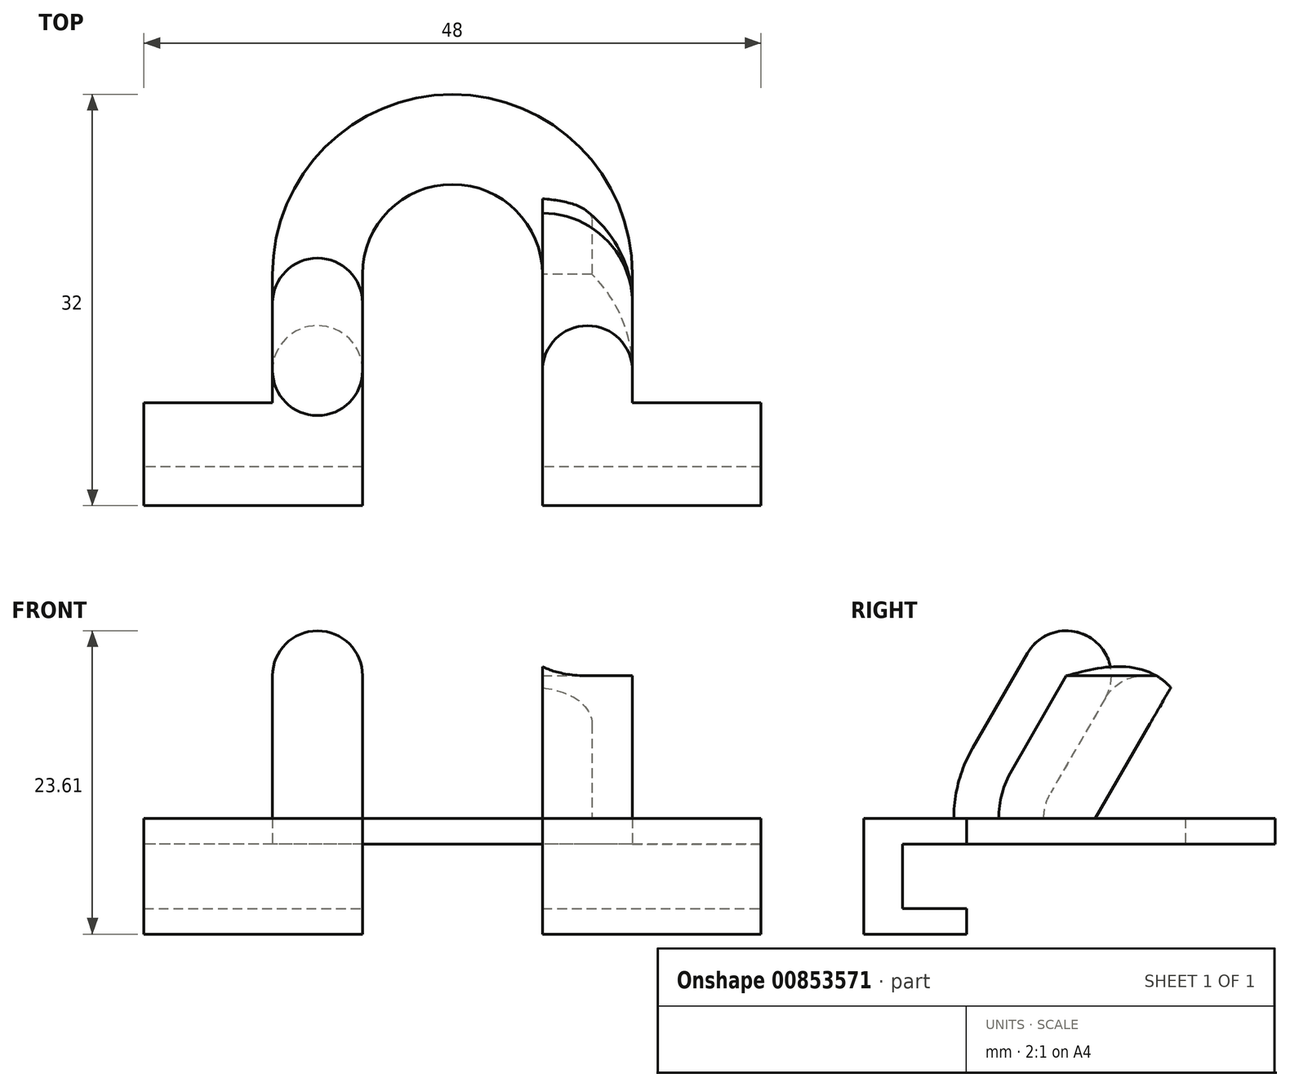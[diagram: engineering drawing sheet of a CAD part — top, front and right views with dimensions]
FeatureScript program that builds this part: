
annotation { "Feature Type Name" : "Feature", "Feature Type Description" : "" }
export const myFeature = defineFeature(function(context is Context, id is Id, definition is map)
    precondition{}
    {
        {
            var Q0;
            Q0=qCreatedBy(makeId("Top.planeOp"),FACE);
            var sketch = newSketch(context, id + "F0", { "sketchPlane" : qUnion([Q0])});
            skLineSegment(sketch, "E0.bottom", {"start": v(0, 0) * mm, "end": v(14, 0) * mm});
            skLineSegment(sketch, "E0.left", {"start": v(0, 0) * mm, "end": v(0, 15) * mm});
            skLineSegment(sketch, "E0.right", {"start": v(14, 0) * mm, "end": v(14, 15) * mm});
            skArc(sketch, "E1", {"start": v(14, 15) * mm, "mid": v(7, 22) * mm, "end": v(0, 15) * mm});
            skArc(sketch, "E2.0", {"start": v(21, 15) * mm, "mid": v(7, 29) * mm, "end": v(-7, 15) * mm});
            skLineSegment(sketch, "E3", {"start": v(0, 0) * mm, "end": v(-7, 0) * mm});
            skLineSegment(sketch, "E4", {"start": v(14, 0) * mm, "end": v(21, 0) * mm});
            skLineSegment(sketch, "E5", {"start": v(21, -3) * mm, "end": v(-7, -3) * mm});
            skLineSegment(sketch, "E6", {"start": v(0, 0) * mm, "end": v(0, -3) * mm});
            skLineSegment(sketch, "E7", {"start": v(14, 0) * mm, "end": v(14, -3) * mm});
            skLineSegment(sketch, "E8", {"start": v(0, 15) * mm, "end": v(-7, 15) * mm});
            skLineSegment(sketch, "E9", {"start": v(21, 15) * mm, "end": v(14, 15) * mm});
            skLineSegment(sketch, "E10", {"start": v(-17, 5) * mm, "end": v(-17, 0) * mm});
            skLineSegment(sketch, "E11", {"start": v(-17, 0) * mm, "end": v(-17, -3) * mm});
            skLineSegment(sketch, "E12", {"start": v(-17, -3) * mm, "end": v(-7, -3) * mm});
            skLineSegment(sketch, "E13", {"start": v(-7, 0) * mm, "end": v(-17, 0) * mm});
            skLineSegment(sketch, "E14", {"start": v(31, 5) * mm, "end": v(31, 0) * mm});
            skLineSegment(sketch, "E15", {"start": v(31, 0) * mm, "end": v(21, 0) * mm});
            skLineSegment(sketch, "E16", {"start": v(31, -3) * mm, "end": v(31, 0) * mm});
            skLineSegment(sketch, "E17", {"start": v(21, -3) * mm, "end": v(31, -3) * mm});
            skLineSegment(sketch, "E18", {"start": v(21, 15) * mm, "end": v(21, 5) * mm});
            skLineSegment(sketch, "E19", {"start": v(21, 5) * mm, "end": v(31, 5) * mm});
            skLineSegment(sketch, "E20", {"start": v(-7, 15) * mm, "end": v(-7, 5) * mm});
            skLineSegment(sketch, "E21", {"start": v(-7, 5) * mm, "end": v(-17, 5) * mm});
            skLineSegment(sketch, "E22", {"start": v(-7, 5) * mm, "end": v(0, 5) * mm});
            skLineSegment(sketch, "E23", {"start": v(21, 5) * mm, "end": v(14, 5) * mm});
            skSolve(sketch);
        }
        {
            var Q0;
            {var subQ0=sQuery(id+"F0.wireOp",EDGE,"E4");Q0=makeQuery(id+"F0.imprint","IMPRINT",FACE,{"disambiguationData":[TD([[makeQuery(id+"F0.imprint","IMPRINT",EDGE,{"derivedFrom":subQ0}),1.0]])]});}
            var Q1;
            {var subQ0=sQuery(id+"F0.wireOp",EDGE,"E3");Q1=makeQuery(id+"F0.imprint","IMPRINT",FACE,{"disambiguationData":[TD([[makeQuery(id+"F0.imprint","IMPRINT",EDGE,{"derivedFrom":subQ0}),-1.0]])]});}
            extrude(context, id + "F1", {"entities" : qUnion([Q0, Q1]), "depth" : 2 * mm, "offsetDistance" : 25 * mm});
        }
        {
            var Q0;
            Q0=makeQuery(id+"F0.imprint","IMPRINT",FACE,{"disambiguationData":[TD([[makeQuery(id+"F0.imprint","IMPRINT",EDGE,{"derivedFrom":sQuery(id+"F0.wireOp",EDGE,"E0.left")}),1.0]])]});
            var Q1;
            Q1=makeQuery(id+"F0.imprint","IMPRINT",FACE,{"disambiguationData":[TD([[makeQuery(id+"F0.imprint","IMPRINT",EDGE,{"derivedFrom":sQuery(id+"F0.wireOp",EDGE,"E1")}),-1.0]])]});
            var Q2;
            Q2=makeQuery(id+"F0.imprint","IMPRINT",FACE,{"disambiguationData":[TD([[makeQuery(id+"F0.imprint","IMPRINT",EDGE,{"derivedFrom":sQuery(id+"F0.wireOp",EDGE,"E0.right")}),-1.0]])]});
            var Q3;
            {var subQ0=sQuery(id+"F0.wireOp",EDGE,"E4");Q3=makeQuery(id+"F0.imprint","IMPRINT",FACE,{"disambiguationData":[TD([[makeQuery(id+"F0.imprint","IMPRINT",EDGE,{"derivedFrom":subQ0}),1.0]])]});}
            var Q4;
            {var subQ0=sQuery(id+"F0.wireOp",EDGE,"E3");Q4=makeQuery(id+"F0.imprint","IMPRINT",FACE,{"disambiguationData":[TD([[makeQuery(id+"F0.imprint","IMPRINT",EDGE,{"derivedFrom":subQ0}),-1.0]])]});}
            extrude(context, id + "F2", {"entities" : qUnion([Q0, Q1, Q2, Q3, Q4]), "depth" : 9 * mm, "offsetDistance" : 25 * mm, "hasSecondDirection" : true, "secondDirectionOppositeDirection" : false, "secondDirectionDepth" : 7 * mm});
        }
        {
            var Q0;
            {var subQ3=sQuery(id+"F0.wireOp",EDGE,"E3");Q0=makeQuery(id+"F0.imprint","IMPRINT",FACE,{"disambiguationData":[TD([[makeQuery(id+"F0.imprint","IMPRINT",EDGE,{"derivedFrom":subQ3}),1.0]])]});}
            var Q1;
            {var subQ3=sQuery(id+"F0.wireOp",EDGE,"E4");Q1=makeQuery(id+"F0.imprint","IMPRINT",FACE,{"disambiguationData":[TD([[makeQuery(id+"F0.imprint","IMPRINT",EDGE,{"derivedFrom":subQ3}),-1.0]])]});}
            extrude(context, id + "F3", {"entities" : qUnion([Q0, Q1]), "depth" : 9 * mm, "offsetDistance" : 25 * mm});
        }
        {
            var Q0;
            Q0=makeQuery(id+"F1.opExtrude","SWEPT_BODY",BODY,{"disambiguationData":[OSD([sQuery(id+"F0.wireOp",EDGE,"E0.left"),sQuery(id+"F0.wireOp",EDGE,"E0.right"),sQuery(id+"F0.wireOp",EDGE,"E1"),sQuery(id+"F0.wireOp",EDGE,"E2.0"),sQuery(id+"F0.wireOp",EDGE,"E2.1"),sQuery(id+"F0.wireOp",EDGE,"E2.3"),sQuery(id+"F0.wireOp",EDGE,"E3"),sQuery(id+"F0.wireOp",EDGE,"E4")])]});
            var Q1;
            Q1=makeQuery(id+"F2.opExtrude","SWEPT_BODY",BODY,{"disambiguationData":[OSD([sQuery(id+"F0.wireOp",EDGE,"E0.left"),sQuery(id+"F0.wireOp",EDGE,"E0.right"),sQuery(id+"F0.wireOp",EDGE,"E1"),sQuery(id+"F0.wireOp",EDGE,"E2.0"),sQuery(id+"F0.wireOp",EDGE,"E2.1"),sQuery(id+"F0.wireOp",EDGE,"E2.3"),sQuery(id+"F0.wireOp",EDGE,"E3"),sQuery(id+"F0.wireOp",EDGE,"E4")])]});
            var Q2;
            Q2=makeQuery(id+"F3.opExtrude","SWEPT_BODY",BODY,{"disambiguationData":[OSD([sQuery(id+"F0.wireOp",EDGE,"E2.1"),sQuery(id+"F0.wireOp",EDGE,"E4"),sQuery(id+"F0.wireOp",EDGE,"E5"),sQuery(id+"F0.wireOp",EDGE,"E7")])]});
            var Q3;
            Q3=makeQuery(id+"F3.opExtrude","SWEPT_BODY",BODY,{"disambiguationData":[OSD([sQuery(id+"F0.wireOp",EDGE,"E2.3"),sQuery(id+"F0.wireOp",EDGE,"E3"),sQuery(id+"F0.wireOp",EDGE,"E5"),sQuery(id+"F0.wireOp",EDGE,"E6")])]});
            booleanBodies(context, id + "F4", {"operationType" : BooleanOperationType.UNION, "tools" : qUnion([Q0, Q1, Q2, Q3])});
        }
        {
            var Q0;
            {var subQ0=sQuery(id+"F0.wireOp",EDGE,"E5");var subQ1=sQuery(id+"F0.wireOp",EDGE,"E3");var subQ2=sQuery(id+"F0.wireOp",EDGE,"E2.3");var subQ3=sQuery(id+"F0.wireOp",EDGE,"E4");var subQ4=sQuery(id+"F0.wireOp",EDGE,"E2.1");Q0=makeQuery(id+"F4.opBoolean","MERGE",FACE,{"derivedFrom":[makeQuery(id+"F2.opExtrude","CAP_FACE",FACE,{"disambiguationData":[OSD([sQuery(id+"F0.wireOp",EDGE,"E0.left"),sQuery(id+"F0.wireOp",EDGE,"E0.right"),sQuery(id+"F0.wireOp",EDGE,"E1"),sQuery(id+"F0.wireOp",EDGE,"E2.0"),subQ4,subQ2,subQ1,subQ3])],"isStart":false}),makeQuery(id+"F3.opExtrude","CAP_FACE",FACE,{"disambiguationData":[OSD([subQ4,subQ3,subQ0,sQuery(id+"F0.wireOp",EDGE,"E7")])],"isStart":false}),makeQuery(id+"F3.opExtrude","CAP_FACE",FACE,{"disambiguationData":[OSD([subQ2,subQ1,subQ0,sQuery(id+"F0.wireOp",EDGE,"E6")])],"isStart":false})]});}
            var sketch = newSketch(context, id + "F5", { "sketchPlane" : qUnion([Q0])});
            skPoint(sketch, "E24", {"position": v(0, 15) * mm});
            skPoint(sketch, "E25", {"position": v(14, 15) * mm});
            skPoint(sketch, "E26", {"position": v(21, 15) * mm});
            skPoint(sketch, "E27", {"position": v(0, -3) * mm});
            skPoint(sketch, "E28", {"position": v(14, -3) * mm});
            skPoint(sketch, "E29", {"position": v(0, 0) * mm});
            skPoint(sketch, "E30", {"position": v(-7, 0) * mm});
            skPoint(sketch, "E31", {"position": v(21, 0) * mm});
            skPoint(sketch, "E32", {"position": v(14, 0) * mm});
            skPoint(sketch, "E33", {"position": v(7, 15) * mm});
            skPoint(sketch, "E34", {"position": v(7, 22) * mm});
            skPoint(sketch, "E35", {"position": v(7, 29) * mm});
            skLineSegment(sketch, "E36", {"start": v(21, 15) * mm, "end": v(14, 15) * mm});
            skPoint(sketch, "E37", {"position": v(17.5, 15) * mm});
            skPoint(sketch, "E38", {"position": v(17.5, 0) * mm});
            skLineSegment(sketch, "E39", {"start": v(17.5, 15) * mm, "end": v(17.5, 0) * mm});
            skCircle(sketch, "E40", {"center": v(17.5, 7.5) * mm, "radius": 3.5 * mm});
            skLineSegment(sketch, "E41", {"start": v(0, 15) * mm, "end": v(21, 15) * mm});
            skLineSegment(sketch, "E42", {"start": v(10.5, 15) * mm, "end": v(10.5, 0) * mm});
            skLineSegment(sketch, "E43", {"start": v(-7, 0) * mm, "end": v(0, 0) * mm});
            skCircle(sketch, "E44", {"center": v(10.5, 7.5) * mm, "radius": 10.5 * mm});
            skLineSegment(sketch, "E45", {"start": v(7, 29) * mm, "end": v(7, -16.59) * mm, "construction": true});
            skPoint(sketch, "E46", {"position": v(-7, 15) * mm});
            skLineSegment(sketch, "E47", {"start": v(-7, 15) * mm, "end": v(0, 15) * mm});
            skLineSegment(sketch, "E48", {"start": v(-7, 15) * mm, "end": v(-7, 0) * mm});
            skLineSegment(sketch, "E49", {"start": v(-3.5, 15) * mm, "end": v(-3.5, 0) * mm});
            skCircle(sketch, "E50", {"center": v(-3.5, 7.5) * mm, "radius": 3.5 * mm});
            skSolve(sketch);
        }
        {
            var Q0;
            {var subQ0=sQuery(id+"F5.wireOp",EDGE,"E44");var subQ1=sQuery(id+"F5.wireOp",EDGE,"E42");var subQ2=makeQuery(id+"F5.imprint","INTERSECT",VERTEX,{"disambiguationData":[OD(0.0)],"derivedFrom":[subQ1,subQ0]});Q0=makeQuery(id+"F5.imprint","IMPRINT",FACE,{"disambiguationData":[TD([[makeQuery(id+"F5.imprint","IMPRINT",EDGE,{"disambiguationData":[TD([[subQ2,-1.0]])],"derivedFrom":subQ1}),1.0]])]});}
            var Q1;
            {var subQ0=sQuery(id+"F5.wireOp",EDGE,"E44");var subQ1=sQuery(id+"F5.wireOp",EDGE,"E42");var subQ2=makeQuery(id+"F5.imprint","INTERSECT",VERTEX,{"disambiguationData":[OD(0.0)],"derivedFrom":[subQ1,subQ0]});Q1=makeQuery(id+"F5.imprint","IMPRINT",FACE,{"disambiguationData":[TD([[makeQuery(id+"F5.imprint","IMPRINT",EDGE,{"disambiguationData":[TD([[subQ2,-1.0]])],"derivedFrom":subQ1}),-1.0]])]});}
            var Q2;
            {var subQ0=sQuery(id+"F5.wireOp",EDGE,"E40");var subQ1=sQuery(id+"F5.wireOp",EDGE,"E39");var subQ2=makeQuery(id+"F5.imprint","INTERSECT",VERTEX,{"disambiguationData":[OD(0.0)],"derivedFrom":[subQ1,subQ0]});Q2=makeQuery(id+"F5.imprint","IMPRINT",FACE,{"disambiguationData":[TD([[makeQuery(id+"F5.imprint","IMPRINT",EDGE,{"disambiguationData":[TD([[subQ2,1.0]])],"derivedFrom":subQ1}),-1.0]])]});}
            var Q3;
            {var subQ0=sQuery(id+"F5.wireOp",EDGE,"E40");var subQ1=sQuery(id+"F5.wireOp",EDGE,"E39");var subQ2=makeQuery(id+"F5.imprint","INTERSECT",VERTEX,{"disambiguationData":[OD(0.0)],"derivedFrom":[subQ1,subQ0]});Q3=makeQuery(id+"F5.imprint","IMPRINT",FACE,{"disambiguationData":[TD([[makeQuery(id+"F5.imprint","IMPRINT",EDGE,{"disambiguationData":[TD([[subQ2,1.0]])],"derivedFrom":subQ1}),1.0]])]});}
            var Q4;
            {var subQ0=sQuery(id+"F5.wireOp",EDGE,"E50");var subQ1=sQuery(id+"F5.wireOp",EDGE,"E49");var subQ2=makeQuery(id+"F5.imprint","INTERSECT",VERTEX,{"disambiguationData":[OD(0.0)],"derivedFrom":[subQ1,subQ0]});Q4=makeQuery(id+"F5.imprint","IMPRINT",FACE,{"disambiguationData":[TD([[makeQuery(id+"F5.imprint","IMPRINT",EDGE,{"disambiguationData":[TD([[subQ2,-1.0]])],"derivedFrom":subQ1}),1.0]])]});}
            var Q5;
            {var subQ0=sQuery(id+"F5.wireOp",EDGE,"E50");var subQ1=sQuery(id+"F5.wireOp",EDGE,"E49");var subQ2=makeQuery(id+"F5.imprint","INTERSECT",VERTEX,{"disambiguationData":[OD(0.0)],"derivedFrom":[subQ1,subQ0]});Q5=makeQuery(id+"F5.imprint","IMPRINT",FACE,{"disambiguationData":[TD([[makeQuery(id+"F5.imprint","IMPRINT",EDGE,{"disambiguationData":[TD([[subQ2,-1.0]])],"derivedFrom":subQ1}),-1.0]])]});}
            var Q6;
            Q6=sQuery(id+"F5.wireOp",EDGE,"E41");
            revolve(context, id + "F6", {"operationType" : NewBodyOperationType.ADD, "surfaceOperationType" : NewSurfaceOperationType.NEW, "entities" : qUnion([Q0, Q1, Q2, Q3, Q4, Q5]), "axis" : qUnion([Q6]), "revolveType" : RevolveType.ONE_DIRECTION, "oppositeDirection" : true, "angle" : 30 * degree});
        }
        {
            var Q0;
            Q0=makeQuery(id+"F6.opRevolve","CAP_FACE",FACE,{"disambiguationData":[OSD([sQuery(id+"F5.wireOp",EDGE,"E40")])],"isStart":false});
            var Q1;
            Q1=makeQuery(id+"F6.opRevolve","CAP_FACE",FACE,{"disambiguationData":[OSD([sQuery(id+"F5.wireOp",EDGE,"E44")])],"isStart":false});
            var Q2;
            Q2=makeQuery(id+"F6.opRevolve","CAP_FACE",FACE,{"disambiguationData":[OSD([sQuery(id+"F5.wireOp",EDGE,"E50")])],"isStart":false});
            extrude(context, id + "F7", {"entities" : qUnion([Q0, Q1, Q2]), "operationType" : NewBodyOperationType.ADD, "depth" : 12 * mm, "offsetDistance" : 25 * mm});
        }
        {
            var Q0;
            Q0=makeQuery(id+"F7.opExtrude","CAP_EDGE",EDGE,{"disambiguationData":[OSD([sQuery(id+"F5.wireOp",EDGE,"E44")])],"isStart":false});
            var Q1;
            Q1=makeQuery(id+"F7.opExtrude","CAP_EDGE",EDGE,{"disambiguationData":[OSD([sQuery(id+"F5.wireOp",EDGE,"E40")])],"isStart":false});
            var Q2;
            Q2=makeQuery(id+"F7.opExtrude","CAP_EDGE",EDGE,{"disambiguationData":[OSD([sQuery(id+"F5.wireOp",EDGE,"E50")])],"isStart":false});
            fillet(context, id + "F8", {"entities" : qUnion([Q0, Q1, Q2]), "radius" : 3.5 * mm, "tangentPropagation" : true, "allowEdgeOverflow" : false});
        }
    });
